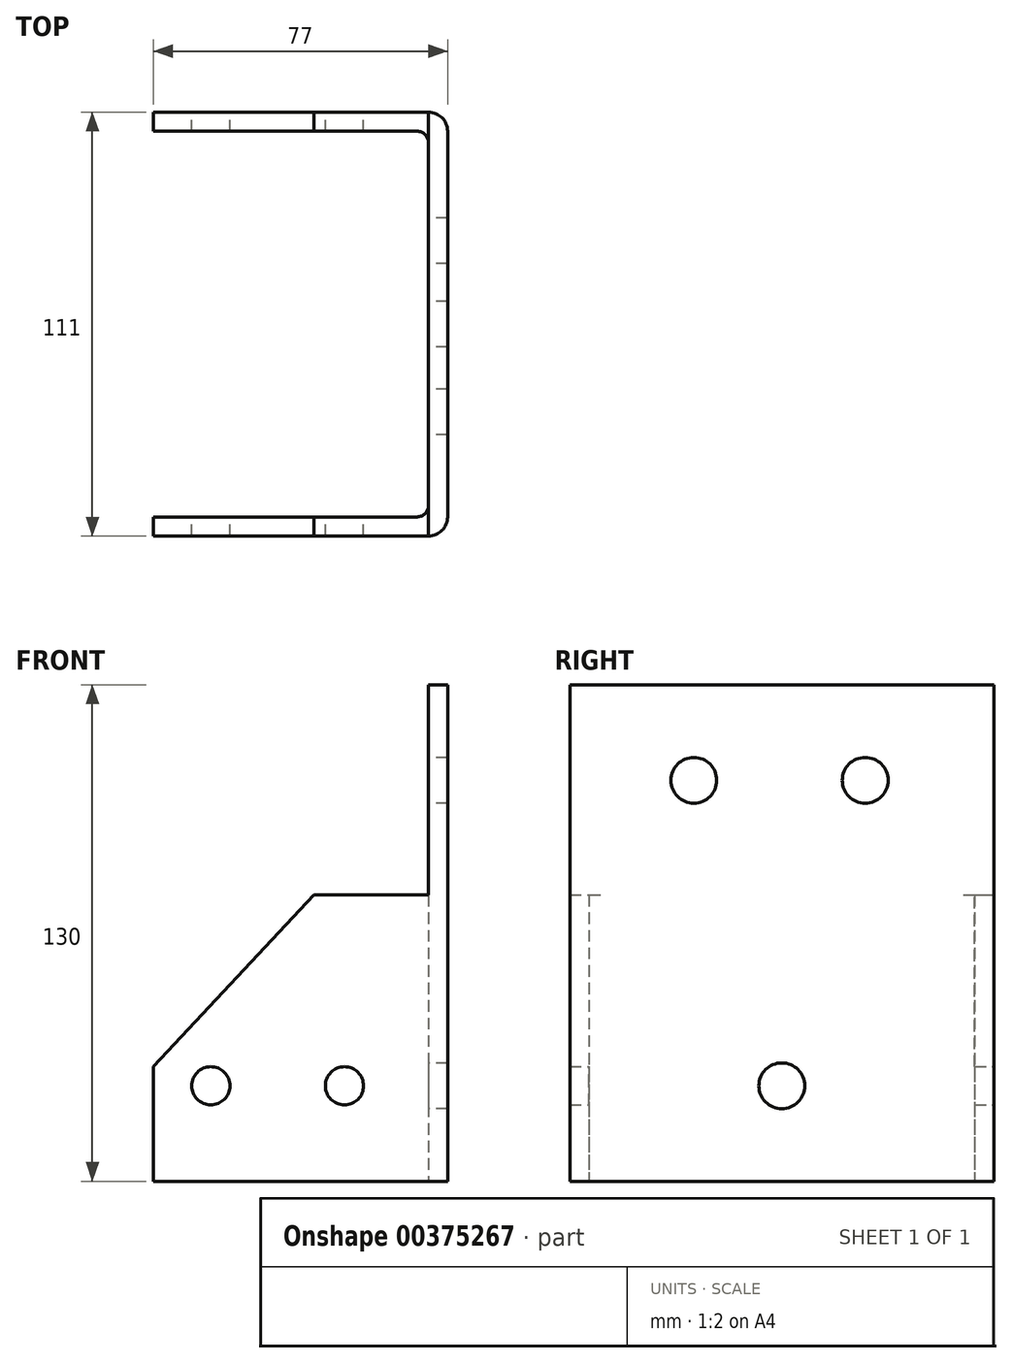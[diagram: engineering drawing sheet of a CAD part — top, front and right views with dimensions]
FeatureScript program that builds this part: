
annotation { "Feature Type Name" : "Feature", "Feature Type Description" : "" }
export const myFeature = defineFeature(function(context is Context, id is Id, definition is map)
    precondition{}
    {
        {
            var Q0;
            Q0=qCreatedBy(makeId("Top.planeOp"),FACE);
            var sketch = newSketch(context, id + "F0", { "sketchPlane" : qUnion([Q0])});
            skLineSegment(sketch, "E0.bottom", {"start": v(-7.53, 71.17) * mm, "end": v(64.47, 71.17) * mm});
            skLineSegment(sketch, "E0.top", {"start": v(-7.53, 66.17) * mm, "end": v(61.47, 66.17) * mm});
            skLineSegment(sketch, "E0.left", {"start": v(-7.53, 71.17) * mm, "end": v(-7.53, 66.17) * mm});
            skLineSegment(sketch, "E0.right", {"start": v(69.47, 66.17) * mm, "end": v(69.47, 66.17) * mm});
            skLineSegment(sketch, "E1.top", {"start": v(64.47, -39.83) * mm, "end": v(64.47, -39.83) * mm});
            skLineSegment(sketch, "E1.left", {"start": v(69.47, 66.17) * mm, "end": v(69.47, -34.83) * mm});
            skLineSegment(sketch, "E1.right", {"start": v(64.47, 63.17) * mm, "end": v(64.47, -31.83) * mm});
            skLineSegment(sketch, "E2.bottom", {"start": v(64.47, -39.83) * mm, "end": v(-7.53, -39.83) * mm});
            skLineSegment(sketch, "E2.top", {"start": v(61.47, -34.83) * mm, "end": v(-7.53, -34.83) * mm});
            skLineSegment(sketch, "E2.right", {"start": v(-7.53, -39.83) * mm, "end": v(-7.53, -34.83) * mm});
            skPoint(sketch, "E3.visualSharp", {"position": v(64.47, 66.17) * mm});
            skArc(sketch, "E3.filletArc", {"start": v(64.47, 63.17) * mm, "mid": v(63.6, 65.3) * mm, "end": v(61.47, 66.17) * mm});
            skPoint(sketch, "E4.visualSharp", {"position": v(69.47, 71.17) * mm});
            skArc(sketch, "E4.filletArc", {"start": v(69.47, 66.17) * mm, "mid": v(68, 69.7) * mm, "end": v(64.47, 71.17) * mm});
            skPoint(sketch, "E5.visualSharp", {"position": v(64.47, -34.83) * mm});
            skArc(sketch, "E5.filletArc", {"start": v(61.47, -34.83) * mm, "mid": v(63.6, -33.95) * mm, "end": v(64.47, -31.83) * mm});
            skPoint(sketch, "E6.visualSharp", {"position": v(69.47, -39.83) * mm});
            skArc(sketch, "E6.filletArc", {"start": v(64.47, -39.83) * mm, "mid": v(68, -38.36) * mm, "end": v(69.47, -34.83) * mm});
            skSolve(sketch);
        }
        {
            var Q0;
            Q0 = qSketchRegion(id + "F0", true);
            extrude(context, id + "F1", {"entities" : qUnion([Q0]), "depth" : 130 * mm});
        }
        {
            var Q0;
            Q0=makeQuery(id+"F1.opExtrude","SWEPT_FACE",FACE,{"disambiguationData":[OSD([sQuery(id+"F0.wireOp",EDGE,"E1.right")])]});
            var sketch = newSketch(context, id + "F2", { "sketchPlane" : qUnion([Q0])});
            skPoint(sketch, "E7", {"position": v(57.82, 0) * mm});
            skPoint(sketch, "E8", {"position": v(2.32, 0) * mm});
            skPoint(sketch, "E9", {"position": v(40, 25) * mm});
            skPoint(sketch, "E10", {"position": v(-71.42, 0) * mm});
            skPoint(sketch, "E11", {"position": v(-53.69, 0) * mm});
            skPoint(sketch, "E12", {"position": v(-71.42, 24.05) * mm});
            skLineSegment(sketch, "E13", {"start": v(42.67, 0) * mm, "end": v(-12.83, 0) * mm});
            skPoint(sketch, "E14", {"position": v(-15.67, 0) * mm});
            skPoint(sketch, "E15", {"position": v(39.75, 0) * mm});
            skPoint(sketch, "E16", {"position": v(-15.67, 25) * mm});
            skCircle(sketch, "E17", {"center": v(-15.67, 25) * mm, "radius": 6 * mm});
            skPoint(sketch, "E18", {"position": v(39.75, 130) * mm});
            skPoint(sketch, "E19", {"position": v(-71.4, 130) * mm});
            skPoint(sketch, "E20", {"position": v(39.97, 105) * mm});
            skPoint(sketch, "E21", {"position": v(7.36, 130) * mm});
            skPoint(sketch, "E22", {"position": v(-37.52, 130) * mm});
            skPoint(sketch, "E23", {"position": v(36.36, 130) * mm});
            skPoint(sketch, "E24", {"position": v(-66.52, 130) * mm});
            skPoint(sketch, "E25", {"position": v(4.25, 130) * mm});
            skPoint(sketch, "E26", {"position": v(7.36, 105) * mm});
            skPoint(sketch, "E27", {"position": v(-37.52, 105) * mm});
            skCircle(sketch, "E28", {"center": v(-37.52, 105) * mm, "radius": 6 * mm});
            skCircle(sketch, "E29", {"center": v(7.36, 105) * mm, "radius": 6 * mm});
            skSolve(sketch);
        }
        {
            var Q0;
            Q0 = qSketchRegion(id + "F2", true);
            extrude(context, id + "F3", {"entities" : qUnion([Q0]), "operationType" : NewBodyOperationType.REMOVE, "oppositeDirection" : true, "depth" : 25 * mm});
        }
        {
            var Q0;
            Q0=makeQuery(id+"F1.opExtrude","SWEPT_FACE",FACE,{"disambiguationData":[OSD([sQuery(id+"F0.wireOp",EDGE,"E0.bottom")])]});
            var sketch = newSketch(context, id + "F4", { "sketchPlane" : qUnion([Q0])});
            skPoint(sketch, "E30", {"position": v(7.53, 0) * mm});
            skPoint(sketch, "E31", {"position": v(-7.47, 0) * mm});
            skPoint(sketch, "E32", {"position": v(7.53, 25) * mm});
            skPoint(sketch, "E33", {"position": v(7.53, 30) * mm});
            skPoint(sketch, "E34", {"position": v(-42.47, 0) * mm});
            skPoint(sketch, "E35", {"position": v(-7.47, 25) * mm});
            skPoint(sketch, "E36", {"position": v(-42.47, 25) * mm});
            skCircle(sketch, "E37", {"center": v(-42.47, 25) * mm, "radius": 5 * mm});
            skCircle(sketch, "E38", {"center": v(-7.47, 25) * mm, "radius": 5 * mm});
            skPoint(sketch, "E39", {"position": v(-64.47, 130) * mm});
            skPoint(sketch, "E40", {"position": v(-34.47, 130) * mm});
            skLineSegment(sketch, "E41", {"start": v(7.53, 30) * mm, "end": v(-34.47, 75) * mm});
            skLineSegment(sketch, "E42", {"start": v(-34.47, 75) * mm, "end": v(-64.47, 75) * mm});
            skLineSegment(sketch, "E43", {"start": v(-64.47, 75) * mm, "end": v(-64.47, 130) * mm});
            skSolve(sketch);
        }
        {
            var Q0;
            Q0 = qSketchRegion(id + "F4", true);
            var Q1;
            {var subQ2=sQuery(id+"F4.wireOp",EDGE,"E41");Q1=makeQuery(id+"F4.imprint","IMPRINT",FACE,{"disambiguationData":[TD([[makeQuery(id+"F4.imprint","IMPRINT",EDGE,{"derivedFrom":subQ2}),-1.0]])]});}
            extrude(context, id + "F5", {"entities" : qUnion([Q0, Q1]), "operationType" : NewBodyOperationType.REMOVE, "endBound" : BoundingType.THROUGH_ALL, "oppositeDirection" : true, "depth" : 25 * mm});
        }
        {
            var Q0;
            Q0 = qSketchRegion(id + "F4", true);
            extrude(context, id + "F6", {"entities" : qUnion([Q0]), "operationType" : NewBodyOperationType.REMOVE, "endBound" : BoundingType.THROUGH_ALL, "oppositeDirection" : true, "depth" : 25 * mm});
        }
    });
